# Revit family: Storage-Vessel_AO_Smith-ST-2000_N
name_source: partatom
category: Mechanical Equipment
revit_build: Autodesk Revit 2016 (Build: 20170117_1200(x64)
units: mm (PartAtom-declared; Revit-internal decimal feet)

## family parameters
Always vertical = Yes
Cut with Voids When Loaded = No
OmniClass Number = 23.75.00.00
OmniClass Title = Climate Control (HVAC)
Part Type = Normal
Room Calculation Point = No
Round Connector Dimension = Use Radius
Shared = No
Work Plane-Based = No

## types (1)
- Storage-Vessel_AO_Smith-ST-2000_N
    1e Maintenance (check-up) = 3 maanden na installatie
    2nd Maintenance (general maintenance) = 12 maanden na installatie
    Assembly Code = D3010
    BIM Content Developer = CAD & Company
    BIM Content Developer URL = http://www.cadcompany.nl
    Cold Water Connection R = 2"
    Description = Voorraadvat
    Destination / Counrty = Nederland
    Diameter (with insulation) = 1300 mm  [stored 4.26509 ft]
    Diameter (without insulation) = 1100 mm  [stored 3.60892 ft]
    Empty Weight = 350.00 kg
    Height (with insulation) = 2175 mm  [stored 7.13583 ft]
    Height (without insulation) = 2061 mm
    Height Cold Water Inlet = 135 mm  [stored 0.442913 ft]
    Height Warm Water Outlet = 2175 mm  [stored 7.13583 ft]
    Hot / Warm Water Connection R = 2"
    Insulation Thickness = 100 mm  [stored 0.328084 ft]
    Maintenance Interval = 12 maanden
    Manufacturer = A.O. Smith Water Products Company b.v.
    Manufacturer Number = E 7110
E 7110
E 7110
    Max. Operating Pressure - tank = 1000000.0 Pa
    Max. Temperature - tank = 95 °C
    Model = ST 2000 N
    Operating Weight = 2230.00 kg
    Packaging Height = 2248 mm  [stored 7.37533 ft]
    Packaging Length = 1426 mm
    Packaging Width = 1170 mm  [stored 3.83858 ft]
    Product Documentation Link = https://www.aosmithinternational.com
    Product Instruction Link = https://www.aosmithinternational.com
    Serial Number = 8717449172282
    Storage Capacity - tank = 1880 m³
    T&P Connection Rp = 2"
    Transport Weight = 440.00 kg
    Type of Packaging = Plastic en Hout
    URL = www.aosmith.nl
    Warranty on Parts = 12 maanden
    Warranty on Tank = 36 maanden
    Workspace Diameter = 2300 mm
    Workspace Height = 3175 mm  [stored 10.4167 ft]

note: [stored X ft] marks values corroborated as IEEE doubles in the binary element streams (Revit-internal decimal feet)

## geometry (parser evidence)
native form markers: Blend x2, Sweep x20
no freeform markers — native parametric forms only
